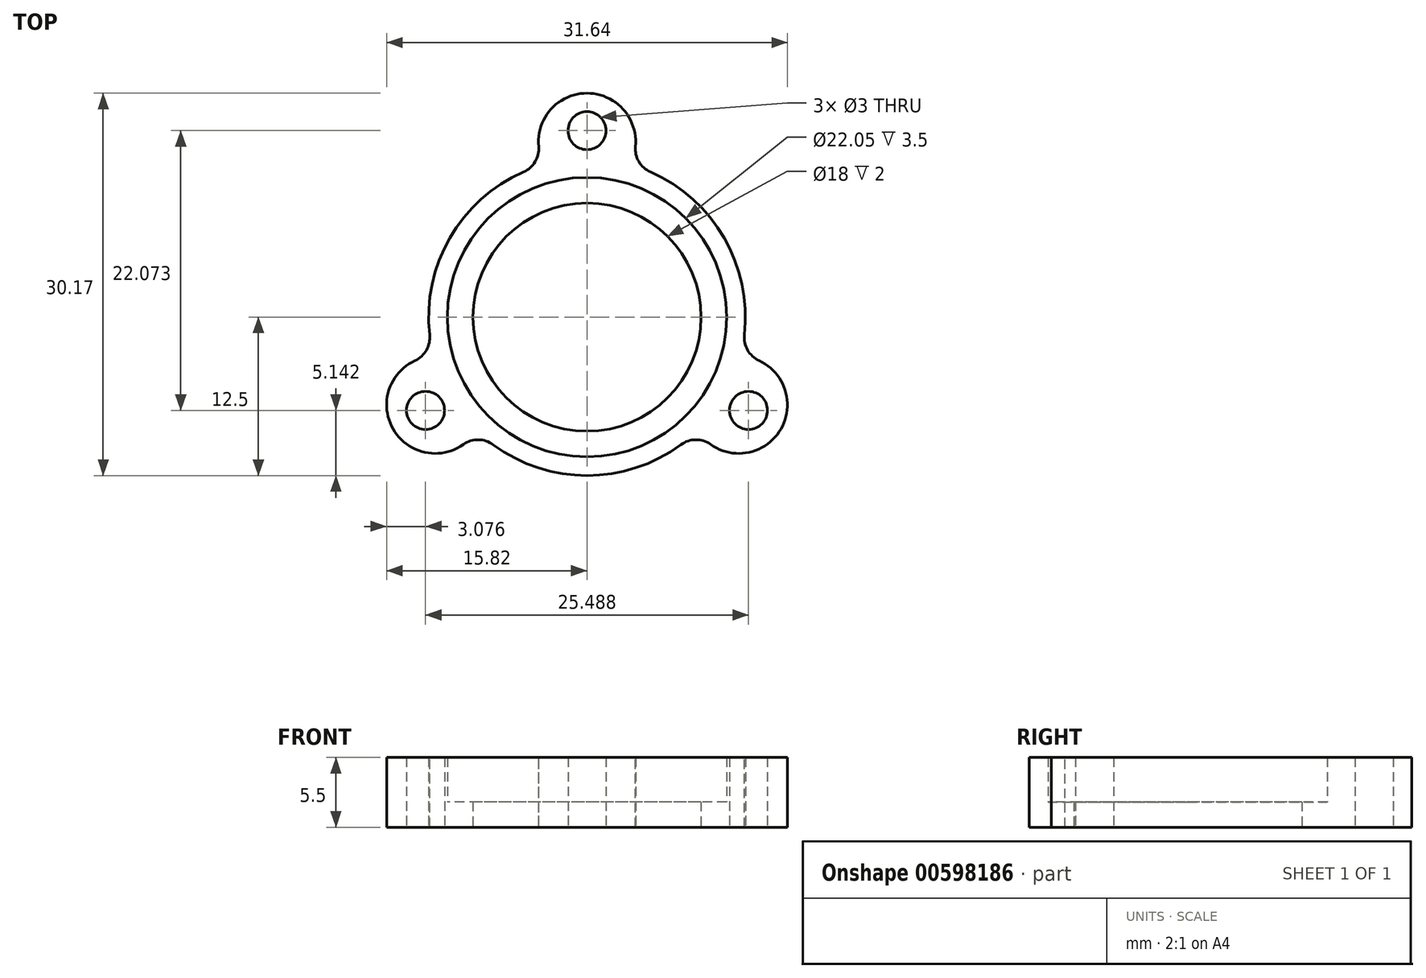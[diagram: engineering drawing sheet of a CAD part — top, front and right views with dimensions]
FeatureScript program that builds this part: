
annotation { "Feature Type Name" : "Feature", "Feature Type Description" : "" }
export const myFeature = defineFeature(function(context is Context, id is Id, definition is map)
    precondition{}
    {
        {
            var Q0;
            Q0=qCreatedBy(makeId("Top.planeOp"),FACE);
            var sketch = newSketch(context, id + "F0", { "sketchPlane" : qUnion([Q0])});
            skCircle(sketch, "E0", {"center": v(0, 0) * mm, "radius": 12.5 * mm});
            skCircle(sketch, "E1", {"center": v(0, 0) * mm, "radius": 11.03 * mm});
            skCircle(sketch, "E2", {"center": v(0, 0) * mm, "radius": 9 * mm});
            skLineSegment(sketch, "E3", {"start": v(0, 16.93) * mm, "end": v(0, 12.5) * mm});
            skCircle(sketch, "E4", {"center": v(0, 14.72) * mm, "radius": 1.5 * mm});
            skLineSegment(sketch, "E5", {"start": v(0, 16.93) * mm, "end": v(0, 18.4) * mm});
            skArc(sketch, "E6", {"start": v(3.39, 12.03) * mm, "mid": v(0, 17.67) * mm, "end": v(-3.39, 12.03) * mm});
            skArc(sketch, "E7.1.0", {"start": v(-12.11, -3.08) * mm, "mid": v(-15.3, -8.83) * mm, "end": v(-8.73, -8.95) * mm});
            skArc(sketch, "E7.2.0", {"start": v(8.73, -8.95) * mm, "mid": v(15.3, -8.83) * mm, "end": v(12.11, -3.08) * mm});
            skCircle(sketch, "E8.1.0", {"center": v(-12.74, -7.36) * mm, "radius": 1.5 * mm});
            skCircle(sketch, "E8.2.0", {"center": v(12.74, -7.36) * mm, "radius": 1.5 * mm});
            skSolve(sketch);
        }
        {
            var Q0;
            {var subQ0=sQuery(id+"F0.wireOp",EDGE,"E7.1.0");Q0=makeQuery(id+"F0.imprint","IMPRINT",FACE,{"disambiguationData":[TD([[makeQuery(id+"F0.imprint","IMPRINT",EDGE,{"derivedFrom":subQ0}),1.0]])]});}
            var Q1;
            Q1=makeQuery(id+"F0.imprint","IMPRINT",FACE,{"disambiguationData":[TD([[makeQuery(id+"F0.imprint","IMPRINT",EDGE,{"derivedFrom":sQuery(id+"F0.wireOp",EDGE,"E1")}),-1.0]])]});
            var Q2;
            {var subQ1=sQuery(id+"F0.wireOp",EDGE,"E3");var subQ4=sQuery(id+"F0.wireOp",EDGE,"E0");var subQ5=makeQuery(id+"F0.imprint","INTERSECT",VERTEX,{"derivedFrom":[subQ4,subQ1]});Q2=makeQuery(id+"F0.imprint","IMPRINT",FACE,{"disambiguationData":[TD([[makeQuery(id+"F0.imprint","IMPRINT",EDGE,{"disambiguationData":[TD([[subQ5,-1.0]])],"derivedFrom":subQ4}),-1.0]])]});}
            var Q3;
            {var subQ1=sQuery(id+"F0.wireOp",EDGE,"E3");var subQ4=sQuery(id+"F0.wireOp",EDGE,"E0");var subQ5=makeQuery(id+"F0.imprint","INTERSECT",VERTEX,{"derivedFrom":[subQ4,subQ1]});Q3=makeQuery(id+"F0.imprint","IMPRINT",FACE,{"disambiguationData":[TD([[makeQuery(id+"F0.imprint","IMPRINT",EDGE,{"disambiguationData":[TD([[subQ5,1.0]])],"derivedFrom":subQ4}),-1.0]])]});}
            var Q4;
            {var subQ0=sQuery(id+"F0.wireOp",EDGE,"E7.2.0");Q4=makeQuery(id+"F0.imprint","IMPRINT",FACE,{"disambiguationData":[TD([[makeQuery(id+"F0.imprint","IMPRINT",EDGE,{"derivedFrom":subQ0}),1.0]])]});}
            extrude(context, id + "F1", {"entities" : qUnion([Q0, Q1, Q2, Q3, Q4]), "depth" : 5.5 * mm, "offsetDistance" : 25 * mm});
        }
        {
            var Q0;
            Q0=makeQuery(id+"F0.imprint","IMPRINT",FACE,{"disambiguationData":[TD([[makeQuery(id+"F0.imprint","IMPRINT",EDGE,{"derivedFrom":sQuery(id+"F0.wireOp",EDGE,"E1")}),1.0]])]});
            extrude(context, id + "F2", {"entities" : qUnion([Q0]), "operationType" : NewBodyOperationType.ADD, "depth" : 2 * mm, "offsetDistance" : 25 * mm});
        }
        {
            var Q0;
            {var subQ0=sQuery(id+"F0.wireOp",EDGE,"E6");var subQ1=sQuery(id+"F0.wireOp",EDGE,"E0");Q0=makeQuery(id+"F1.opExtrude","SWEPT_EDGE",EDGE,{"disambiguationData":[OSD([subQ1,subQ0]),TDD([makeQuery(id+"F0.imprint","INTERSECT",VERTEX,{"disambiguationData":[OD(0.0)],"derivedFrom":[subQ1,subQ0]})])]});}
            var Q1;
            {var subQ0=sQuery(id+"F0.wireOp",EDGE,"E7.2.0");var subQ1=sQuery(id+"F0.wireOp",EDGE,"E0");Q1=makeQuery(id+"F1.opExtrude","SWEPT_EDGE",EDGE,{"disambiguationData":[OSD([subQ1,subQ0]),TDD([makeQuery(id+"F0.imprint","INTERSECT",VERTEX,{"disambiguationData":[OD(1.0)],"derivedFrom":[subQ1,subQ0]})])]});}
            var Q2;
            {var subQ0=sQuery(id+"F0.wireOp",EDGE,"E7.1.0");var subQ1=sQuery(id+"F0.wireOp",EDGE,"E0");Q2=makeQuery(id+"F1.opExtrude","SWEPT_EDGE",EDGE,{"disambiguationData":[OSD([subQ1,subQ0]),TDD([makeQuery(id+"F0.imprint","INTERSECT",VERTEX,{"disambiguationData":[OD(0.0)],"derivedFrom":[subQ1,subQ0]})])]});}
            var Q3;
            {var subQ0=sQuery(id+"F0.wireOp",EDGE,"E6");var subQ1=sQuery(id+"F0.wireOp",EDGE,"E0");Q3=makeQuery(id+"F1.opExtrude","SWEPT_EDGE",EDGE,{"disambiguationData":[OSD([subQ1,subQ0]),TDD([makeQuery(id+"F0.imprint","INTERSECT",VERTEX,{"disambiguationData":[OD(1.0)],"derivedFrom":[subQ1,subQ0]})])]});}
            var Q4;
            {var subQ0=sQuery(id+"F0.wireOp",EDGE,"E7.1.0");var subQ1=sQuery(id+"F0.wireOp",EDGE,"E0");Q4=makeQuery(id+"F1.opExtrude","SWEPT_EDGE",EDGE,{"disambiguationData":[OSD([subQ1,subQ0]),TDD([makeQuery(id+"F0.imprint","INTERSECT",VERTEX,{"disambiguationData":[OD(1.0)],"derivedFrom":[subQ1,subQ0]})])]});}
            var Q5;
            {var subQ0=sQuery(id+"F0.wireOp",EDGE,"E7.2.0");var subQ1=sQuery(id+"F0.wireOp",EDGE,"E0");Q5=makeQuery(id+"F1.opExtrude","SWEPT_EDGE",EDGE,{"disambiguationData":[OSD([subQ1,subQ0]),TDD([makeQuery(id+"F0.imprint","INTERSECT",VERTEX,{"disambiguationData":[OD(0.0)],"derivedFrom":[subQ1,subQ0]})])]});}
            fillet(context, id + "F3", {"entities" : qUnion([Q0, Q1, Q2, Q3, Q4, Q5]), "radius" : 2 * mm, "tangentPropagation" : true, "allowEdgeOverflow" : false});
        }
    });
